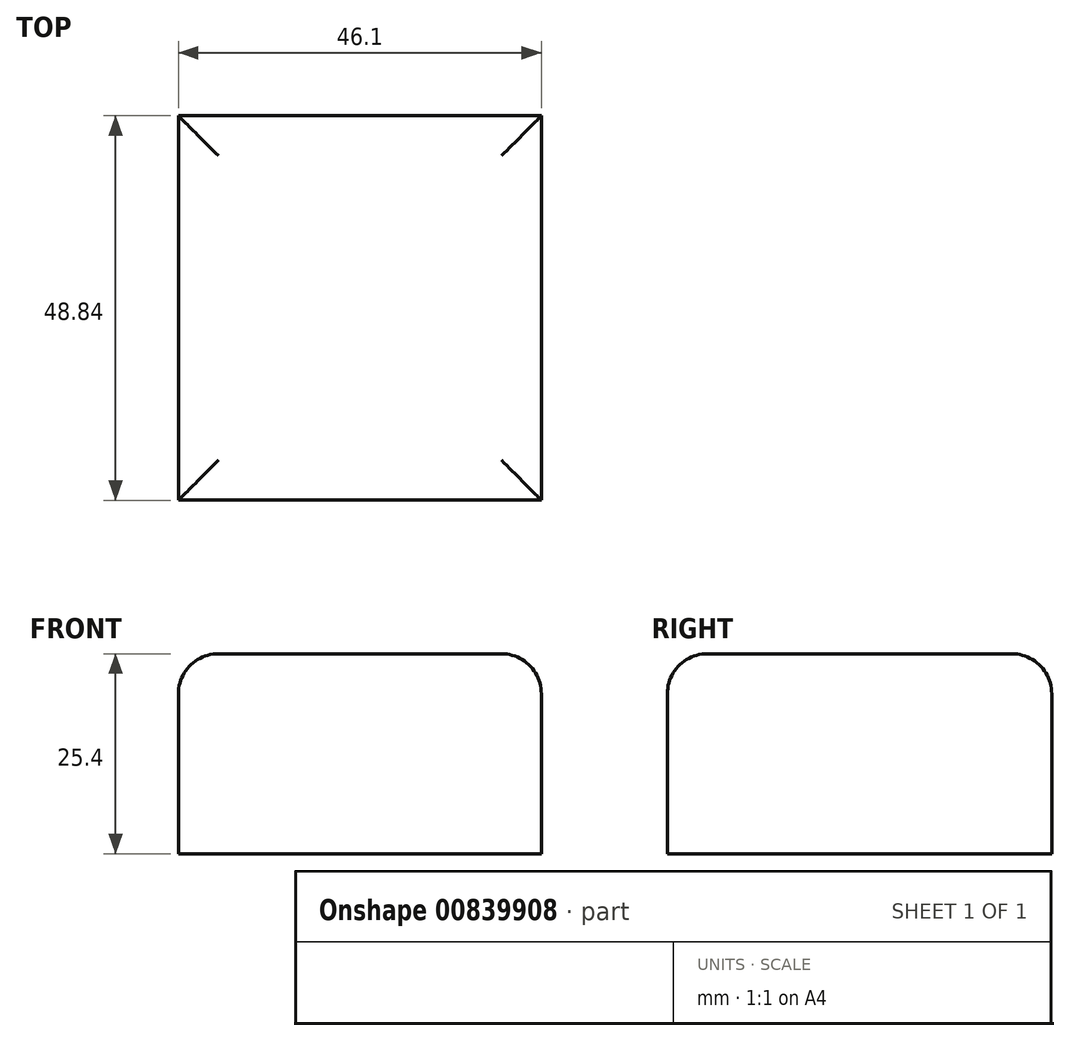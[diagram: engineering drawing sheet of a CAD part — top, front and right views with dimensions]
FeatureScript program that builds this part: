
annotation { "Feature Type Name" : "Feature", "Feature Type Description" : "" }
export const myFeature = defineFeature(function(context is Context, id is Id, definition is map)
    precondition{}
    {
        {
            var Q0;
            Q0=qCreatedBy(makeId("Top.planeOp"),FACE);
            var sketch = newSketch(context, id + "F0", { "sketchPlane" : qUnion([Q0])});
            skLineSegment(sketch, "E0.bottom", {"start": v(23.05, 24.42) * mm, "end": v(-23.05, 24.42) * mm});
            skLineSegment(sketch, "E0.top", {"start": v(23.05, -24.42) * mm, "end": v(-23.05, -24.42) * mm});
            skLineSegment(sketch, "E0.left", {"start": v(23.05, 24.42) * mm, "end": v(23.05, -24.42) * mm});
            skLineSegment(sketch, "E0.right", {"start": v(-23.05, 24.42) * mm, "end": v(-23.05, -24.42) * mm});
            skPoint(sketch, "E0.middle", {"position": v(0, 0) * mm});
            skSolve(sketch);
        }
        {
            var Q0;
            Q0=makeQuery(id+"F0.imprint","IMPRINT",FACE,{"disambiguationData":[TD([[makeQuery(id+"F0.imprint","IMPRINT",EDGE,{"derivedFrom":sQuery(id+"F0.wireOp",EDGE,"E0.bottom")}),1.0]])]});
            extrude(context, id + "F1", {"entities" : qUnion([Q0]), "depth" : 25.4 * mm, "offsetDistance" : 25.4 * mm});
        }
        {
            var Q0;
            Q0=makeQuery(id+"F1.opExtrude","CAP_EDGE",EDGE,{"disambiguationData":[OSD([sQuery(id+"F0.wireOp",EDGE,"E0.top")])],"isStart":false});
            var Q1;
            Q1=makeQuery(id+"F1.opExtrude","CAP_EDGE",EDGE,{"disambiguationData":[OSD([sQuery(id+"F0.wireOp",EDGE,"E0.right")])],"isStart":false});
            var Q2;
            Q2=makeQuery(id+"F1.opExtrude","CAP_EDGE",EDGE,{"disambiguationData":[OSD([sQuery(id+"F0.wireOp",EDGE,"E0.bottom")])],"isStart":false});
            var Q3;
            Q3=makeQuery(id+"F1.opExtrude","CAP_EDGE",EDGE,{"disambiguationData":[OSD([sQuery(id+"F0.wireOp",EDGE,"E0.left")])],"isStart":false});
            fillet(context, id + "F2", {"entities" : qUnion([Q0, Q1, Q2, Q3]), "radius" : 5.08 * mm, "tangentPropagation" : true, "allowEdgeOverflow" : false});
        }
    });
